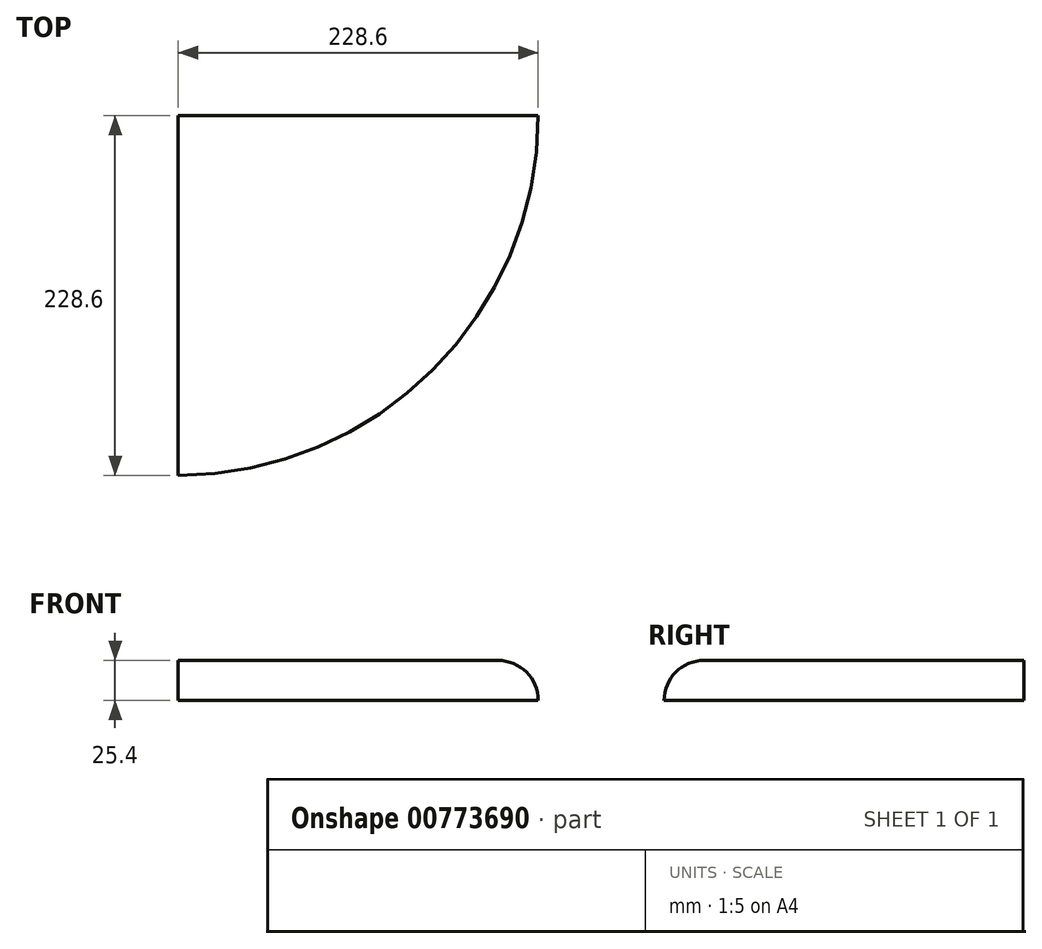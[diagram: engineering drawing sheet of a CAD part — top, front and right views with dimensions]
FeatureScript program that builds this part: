
annotation { "Feature Type Name" : "Feature", "Feature Type Description" : "" }
export const myFeature = defineFeature(function(context is Context, id is Id, definition is map)
    precondition{}
    {
        {
            var Q0;
            Q0=qCreatedBy(makeId("Top.planeOp"),FACE);
            var sketch = newSketch(context, id + "F0", { "sketchPlane" : qUnion([Q0])});
            skCircle(sketch, "E0", {"center": v(0, 0) * mm, "radius": 228.6 * mm});
            skSolve(sketch);
        }
        {
            var Q0;
            Q0=makeQuery(id+"F0.imprint","IMPRINT",FACE,{"disambiguationData":[TD([[makeQuery(id+"F0.imprint","IMPRINT",EDGE,{"derivedFrom":sQuery(id+"F0.wireOp",EDGE,"E0")}),1.0]])]});
            var sketch = newSketch(context, id + "F1", { "sketchPlane" : qUnion([Q0])});
            skLineSegment(sketch, "E1", {"start": v(0, 0) * mm, "end": v(0, 228.6) * mm});
            skLineSegment(sketch, "E2", {"start": v(0, 0) * mm, "end": v(228.6, 0) * mm});
            skLineSegment(sketch, "E3", {"start": v(0, 228.6) * mm, "end": v(0, -228.6) * mm});
            skLineSegment(sketch, "E4", {"start": v(228.6, 0) * mm, "end": v(-228.6, 0) * mm});
            skLineSegment(sketch, "E5", {"start": v(0, 0) * mm, "end": v(161.64, 161.64) * mm});
            skLineSegment(sketch, "E6.0", {"start": v(20.2, -20.2) * mm, "end": v(181.85, 141.44) * mm});
            skLineSegment(sketch, "E7.0", {"start": v(40.41, -40.41) * mm, "end": v(202.06, 121.23) * mm});
            skLineSegment(sketch, "E8.0", {"start": v(60.62, -60.62) * mm, "end": v(222.26, 101.03) * mm});
            skLineSegment(sketch, "E9.0", {"start": v(80.82, -80.82) * mm, "end": v(242.47, 80.82) * mm});
            skLineSegment(sketch, "E10.0", {"start": v(101.03, -101.03) * mm, "end": v(262.67, 60.62) * mm});
            skLineSegment(sketch, "E11.0", {"start": v(-20.2, 20.2) * mm, "end": v(141.44, 181.85) * mm});
            skLineSegment(sketch, "E12.0", {"start": v(-40.41, 40.41) * mm, "end": v(121.23, 202.06) * mm});
            skLineSegment(sketch, "E13.0", {"start": v(-60.62, 60.62) * mm, "end": v(101.03, 222.26) * mm});
            skLineSegment(sketch, "E14.0", {"start": v(-80.82, 80.82) * mm, "end": v(80.82, 242.47) * mm});
            skLineSegment(sketch, "E15.0", {"start": v(-101.03, 101.03) * mm, "end": v(60.62, 262.67) * mm});
            skCircle(sketch, "E16", {"center": v(0, 0) * mm, "radius": 228.6 * mm});
            skSolve(sketch);
        }
        {
            var Q0;
            {var subQ0=sQuery(id+"F1.wireOp",EDGE,"E15.0");var subQ1=sQuery(id+"F1.wireOp",EDGE,"E3");var subQ2=makeQuery(id+"F1.imprint","INTERSECT",VERTEX,{"derivedFrom":[subQ1,subQ0]});Q0=makeQuery(id+"F1.imprint","IMPRINT",FACE,{"disambiguationData":[TD([[makeQuery(id+"F1.imprint","IMPRINT",EDGE,{"disambiguationData":[TD([[subQ2,-1.0]])],"derivedFrom":subQ1}),1.0]])]});}
            extrude(context, id + "F2", {"entities" : qUnion([Q0]), "depth" : 25.4 * mm, "offsetDistance" : 25.4 * mm});
        }
        {
            var Q0;
            Q0=makeQuery(id+"F2.opExtrude","CAP_EDGE",EDGE,{"disambiguationData":[OSD([sQuery(id+"F1.wireOp",EDGE,"E16")])],"isStart":false});
            fillet(context, id + "F3", {"entities" : qUnion([Q0]), "radius" : 25.4 * mm, "tangentPropagation" : true, "allowEdgeOverflow" : false});
        }
    });
